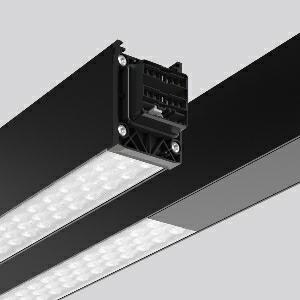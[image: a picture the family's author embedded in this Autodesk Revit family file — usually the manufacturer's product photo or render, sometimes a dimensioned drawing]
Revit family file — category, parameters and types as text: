
# Revit family: linedo_2_3m_30_1100_952330_853_776_503_a28f
name_source: partatom
category: Lighting Fixtures
units: mm (PartAtom-declared; Revit-internal decimal feet)

## family parameters
Cut with Voids When Loaded = No
Host = Face
Light Source = No
Part Type = Normal
Room Calculation Point = No
Round Connector Dimension = Use Diameter
Shared = No

## types (1)
- LINEDO_2,3m_30_1100 (1 x LED Modul 850, 4100 lm, 5000)
    Apparent Load = 54 VA
    CIE Flux Codes = 89 97 99 100 100
    Color Rendering = 80
    Color Temperature = 5000
    Default Elevation = 1800 mm
    Description = LINEDO, 54 W, 8200 lm, 850, black, DALI
Continuous line luminaire, L 2291 B 58 H 76
    Height = 76 mm
    Lamp = 1 x LED Modul 850
    Lamp Light Flux = 4100 lm
    Lamp count = 1
    Length = 2291 mm
    Lifetime = 50000 h
    Luminous efficacy = 152 lm/W
    Manufacturer = RZB
    ModVariant = No
    Model = 952330.853.776.503
    Mounting Place = Ceiling
    Mounting Type = Surface mounted, Pendant
    Number of Poles = 1
    OnlyDefault = Yes
    Power Factor = 1
    Product Name = LINEDO_2,3m_30_1100
    Product group = Continuous line luminaire system Linedo IP 54
    ProductGroupID = 314
    Protection Class = Protection class I
    Protection Degree = IP 54
    RLX_Detail_Level = 1
    RLX_Emergency_Light_Flux = 0 lm
    RLX_Emergency_Type = 0
    RLX_Emergency_Type_DB = No
    RlxData = <blob elided: 56581 chars, md5=c636c7c7>
    Socket = socket
    Standby Power = 0 W
    System Light Flux = 8200 lm
    System Power = 54 W
    Type Comments = Product without accessories
    Type Image = 954530.853.476.504.jpg
    URL = http://relux.com
    VarID = ---
    Voltage = 230 V
    Voltage Range = 220-240 V
    Weight = 0.00 kg
    Width = 58 mm

## geometry (parser evidence)
native form markers: Blend x4, Sweep x14
no freeform markers — native parametric forms only
